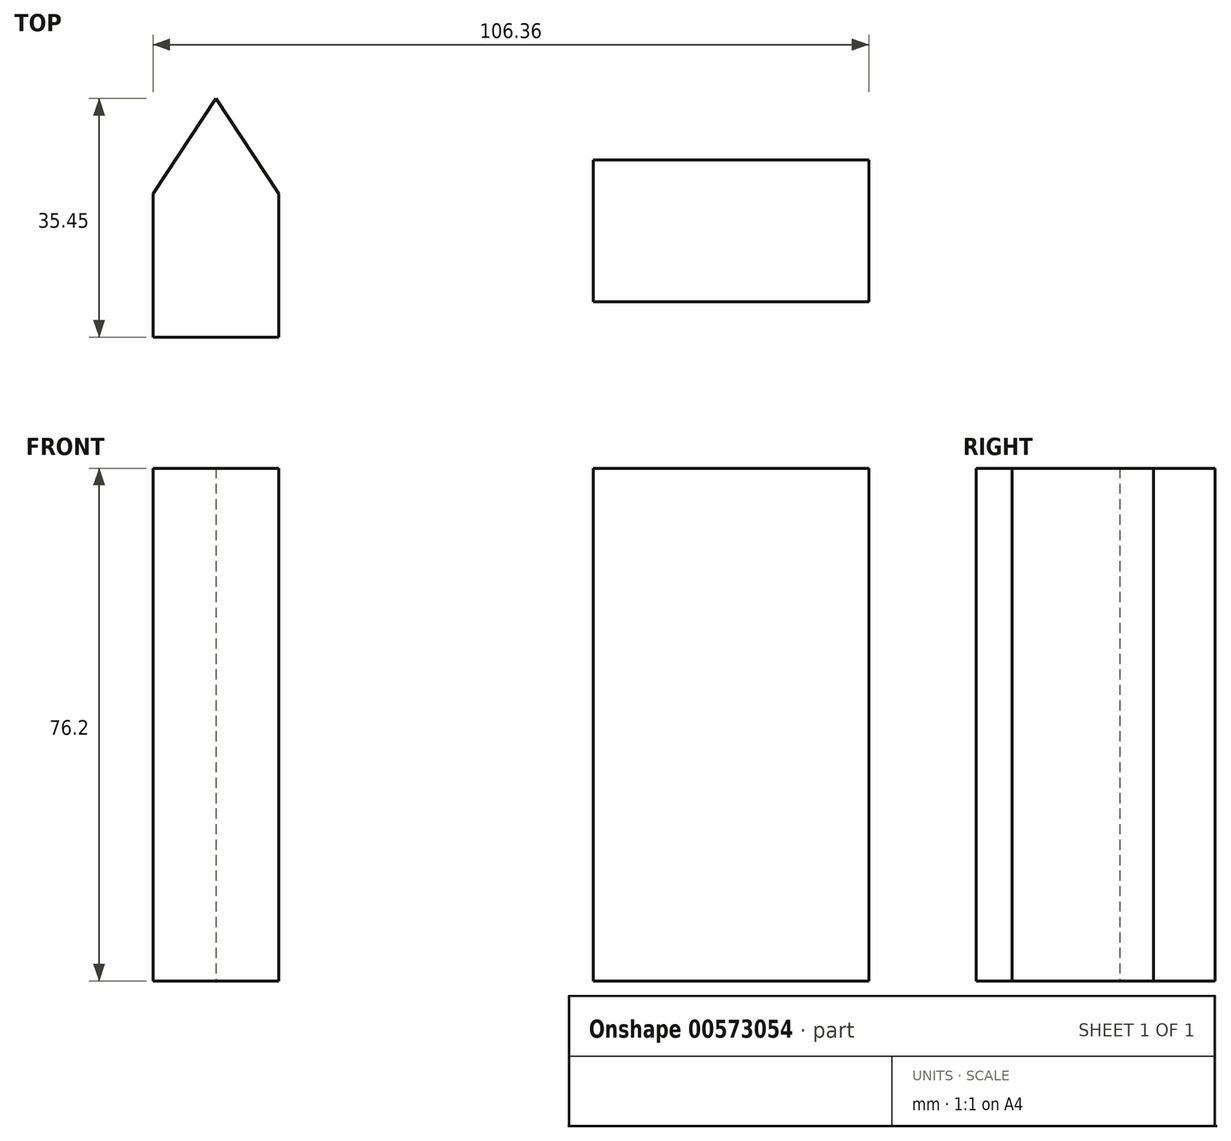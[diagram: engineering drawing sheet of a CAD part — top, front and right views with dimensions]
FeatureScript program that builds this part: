
annotation { "Feature Type Name" : "Feature", "Feature Type Description" : "" }
export const myFeature = defineFeature(function(context is Context, id is Id, definition is map)
    precondition{}
    {
        {
            var Q0;
            Q0=qCreatedBy(makeId("Top.planeOp"),FACE);
            var sketch = newSketch(context, id + "F0", { "sketchPlane" : qUnion([Q0])});
            skLineSegment(sketch, "E0.bottom", {"start": v(4.8, 44.32) * mm, "end": v(45.75, 44.32) * mm});
            skLineSegment(sketch, "E0.top", {"start": v(4.8, 23.24) * mm, "end": v(45.75, 23.24) * mm});
            skLineSegment(sketch, "E0.left", {"start": v(4.8, 44.32) * mm, "end": v(4.8, 23.24) * mm});
            skLineSegment(sketch, "E0.right", {"start": v(45.75, 44.32) * mm, "end": v(45.75, 23.24) * mm});
            skSolve(sketch);
        }
        {
            var Q0;
            Q0=makeQuery(id+"F0.imprint","IMPRINT",FACE,{"disambiguationData":[TD([[makeQuery(id+"F0.imprint","IMPRINT",EDGE,{"derivedFrom":sQuery(id+"F0.wireOp",EDGE,"E0.bottom")}),-1.0]])]});
            extrude(context, id + "F1", {"entities" : qUnion([Q0]), "depth" : 76.2 * mm, "offsetDistance" : 25.4 * mm});
        }
        {
            var Q0;
            Q0=qCreatedBy(makeId("Top.planeOp"),FACE);
            var sketch = newSketch(context, id + "F2", { "sketchPlane" : qUnion([Q0])});
            skLineSegment(sketch, "E1.bottom", {"start": v(-60.6, 39.29) * mm, "end": v(-41.92, 39.29) * mm});
            skLineSegment(sketch, "E1.top", {"start": v(-60.6, 17.97) * mm, "end": v(-41.92, 17.97) * mm});
            skLineSegment(sketch, "E1.left", {"start": v(-60.6, 39.29) * mm, "end": v(-60.6, 17.97) * mm});
            skLineSegment(sketch, "E1.right", {"start": v(-41.92, 39.29) * mm, "end": v(-41.92, 17.97) * mm});
            skLineSegment(sketch, "E2", {"start": v(-60.6, 39.29) * mm, "end": v(-51.26, 53.42) * mm});
            skLineSegment(sketch, "E3", {"start": v(-51.26, 53.42) * mm, "end": v(-41.92, 39.29) * mm});
            skSolve(sketch);
        }
        {
            var Q0;
            Q0=makeQuery(id+"F2.imprint","IMPRINT",FACE,{"disambiguationData":[TD([[makeQuery(id+"F2.imprint","IMPRINT",EDGE,{"derivedFrom":sQuery(id+"F2.wireOp",EDGE,"E1.bottom")}),-1.0]])]});
            var Q1;
            Q1=makeQuery(id+"F2.imprint","IMPRINT",FACE,{"disambiguationData":[TD([[makeQuery(id+"F2.imprint","IMPRINT",EDGE,{"derivedFrom":sQuery(id+"F2.wireOp",EDGE,"E1.bottom")}),1.0]])]});
            extrude(context, id + "F3", {"entities" : qUnion([Q0, Q1]), "depth" : 76.2 * mm, "offsetDistance" : 25.4 * mm});
        }
    });
